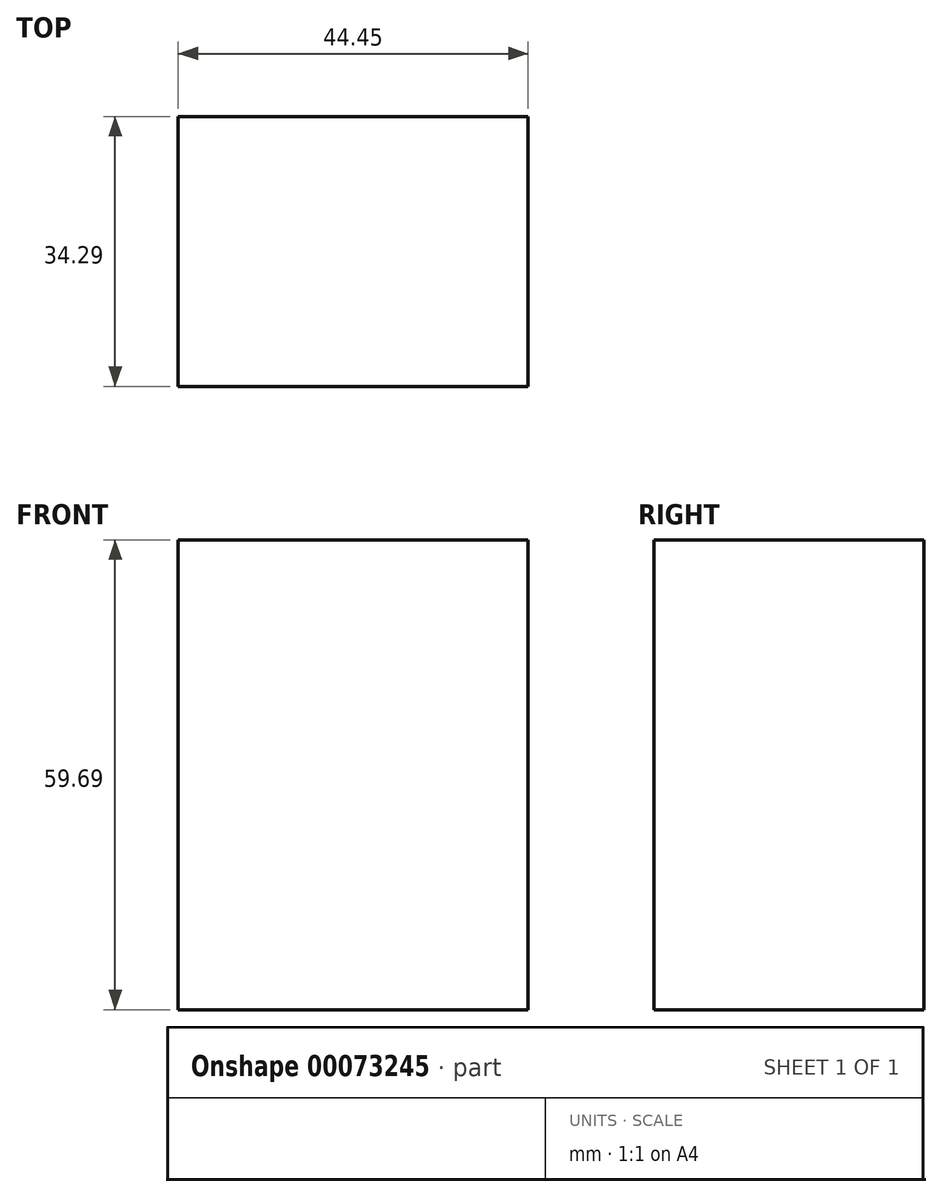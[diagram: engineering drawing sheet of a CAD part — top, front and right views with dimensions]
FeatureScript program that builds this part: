
annotation { "Feature Type Name" : "Feature", "Feature Type Description" : "" }
export const myFeature = defineFeature(function(context is Context, id is Id, definition is map)
    precondition{}
    {
        {
            var Q0;
            Q0=qCreatedBy(makeId("Front.planeOp"),FACE);
            var sketch = newSketch(context, id + "F0", { "sketchPlane" : qUnion([Q0])});
            skLineSegment(sketch, "E0.bottom", {"start": v(0, 0) * mm, "end": v(44.45, 0) * mm});
            skLineSegment(sketch, "E0.top", {"start": v(0, 59.7) * mm, "end": v(44.45, 59.7) * mm});
            skLineSegment(sketch, "E0.left", {"start": v(0, 0) * mm, "end": v(0, 59.7) * mm});
            skLineSegment(sketch, "E0.right", {"start": v(44.45, 0) * mm, "end": v(44.45, 59.7) * mm});
            skSolve(sketch);
        }
        {
            var Q0;
            Q0=makeQuery(id+"F0.imprint","IMPRINT",FACE,{"disambiguationData":[TD([[makeQuery(id+"F0.imprint","IMPRINT",EDGE,{"derivedFrom":sQuery(id+"F0.wireOp",EDGE,"E0.bottom")}),1.0]])]});
            extrude(context, id + "F1", {"entities" : qUnion([Q0]), "depth" : 34.3 * mm});
        }
    });
